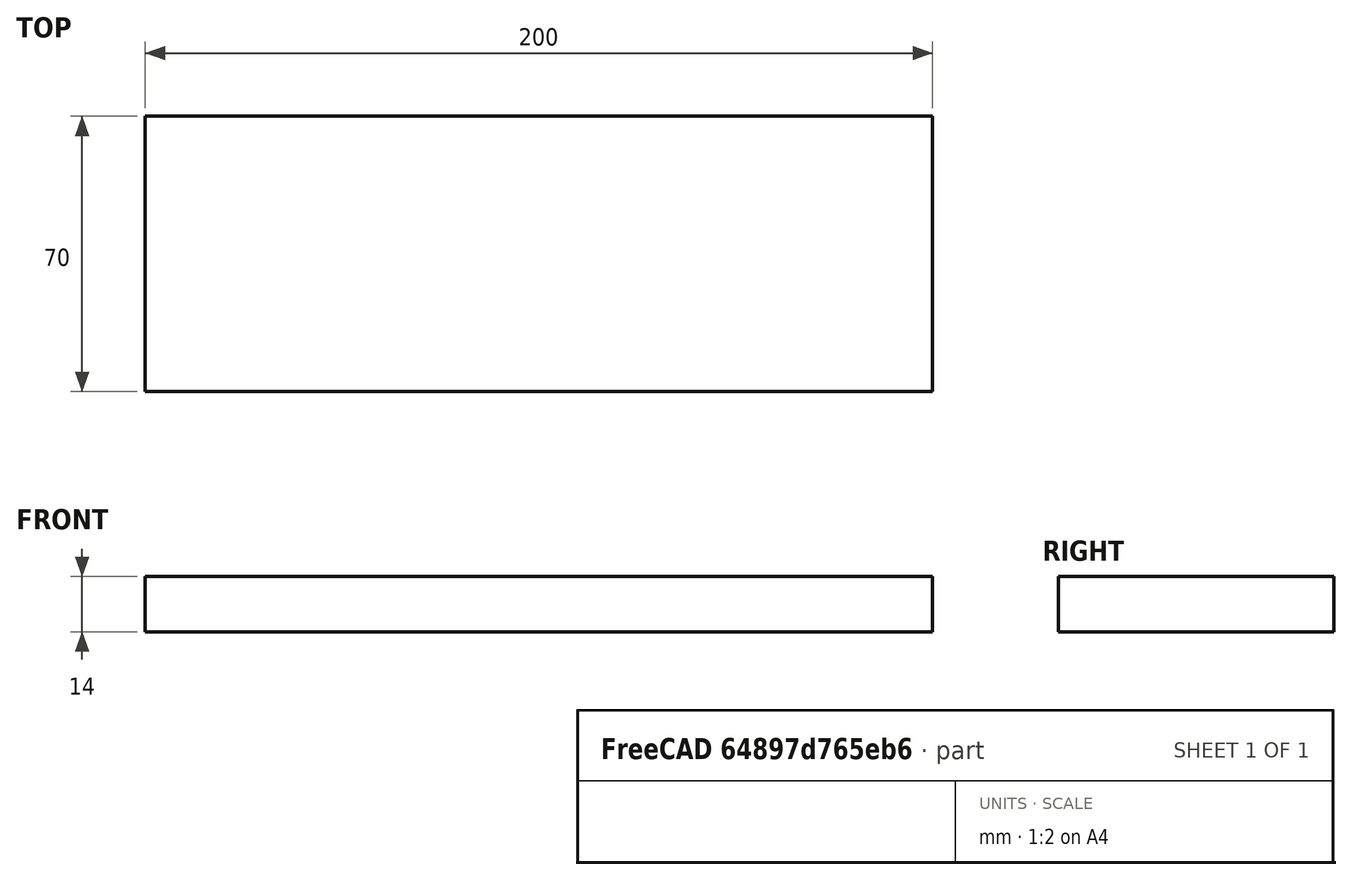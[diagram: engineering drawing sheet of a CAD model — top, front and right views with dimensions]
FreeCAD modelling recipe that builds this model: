
FCSTD DOCUMENT  (FreeCAD 0.19R24276 (Git))
Label: Plate_200x70
License: All rights reserved
LicenseURL: http://en.wikipedia.org/wiki/All_rights_reserved
objects: Sketcher::SketchObject×1, PartDesign::Pad×1, PartDesign::Body×1
note: 4 computed .brp shape members not serialized (recipe doc carries the construction recipe); baked Part::Feature solids carry a one-line shape summary decoded from their .brp

FEATURE [Sketcher::SketchObject] Sketch
  FullyConstrained = true
  MapMode = 5
  Support = -> [XY_Plane]
  sketch-geometry (4):
    g0: LineSegment StartX=0 StartY=0 StartZ=0 EndX=200 EndY=0 EndZ=0
    g1: LineSegment StartX=200 StartY=0 StartZ=0 EndX=200 EndY=70 EndZ=0
    g2: LineSegment StartX=200 StartY=70 StartZ=0 EndX=0 EndY=70 EndZ=0
    g3: LineSegment StartX=0 StartY=70 StartZ=0 EndX=0 EndY=0 EndZ=0
  constraints (11):
    c: Coincident(g0,g1)
    c: Coincident(g1,g2)
    c: Coincident(g2,g3)
    c: Coincident(g3,g0)
    c: Horizontal(g0)
    c: Horizontal(g2)
    c: Vertical(g1)
    c: Vertical(g3)
    c: Coincident(g0,g-1)
    c: DistanceY(g1,g1) = 70
    c: DistanceX(g0,g0) = 200
FEATURE [PartDesign::Pad] Pad
  Direction = (1,1,1)
  Length = 14
  Length2 = 100
  Profile = -> Sketch
  Type = 0
FEATURE [PartDesign::Body] Body
  Group = -> [Sketch,Pad]
  Origin = -> Origin
  Tip = -> Pad
